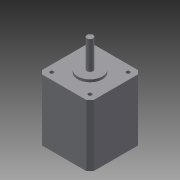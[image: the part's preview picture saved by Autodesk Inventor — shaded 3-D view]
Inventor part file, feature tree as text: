
AUTODESK INVENTOR PART (.ipt)
format: ipt  version: 2013 SP2 (Build 170200200, 200)  size: 102,912 bytes
history: native  units: mm
features: extrude x3, sketch x3, chamfer x1
ambient origin geometry x8: Origin, YZ Plane, XZ Plane, XY Plane, X Axis, Y Axis, Z Axis, Center Point
bodies: Solid1 (feature_tree)
feature tree (7):
  extrude  "Extrusion1"  Depth=42.0mm
  chamfer  "Chamfer1"  Distance=3.0mm
  sketch  "Sketch2"  dims[d2=31.0mm]
  extrude  "Extrusion2"  Depth=3.0mm
  extrude  "Extrusion3"  Depth=3.0mm
  sketch  "Sketch1"  dims[d0=42.0mm d1=42.0mm]
  sketch  "Sketch3"  dims[d3=3.0mm d4=3.0mm d5=3.0mm d6=3.0mm d7=50.0mm d8=0.0mm d9=5.0mm d10=3.0mm d11=2.0mm d12=45.0deg d13=20.0mm d14=25.0mm d15=0.0mm d16=2.0mm d17=0.0mm]
